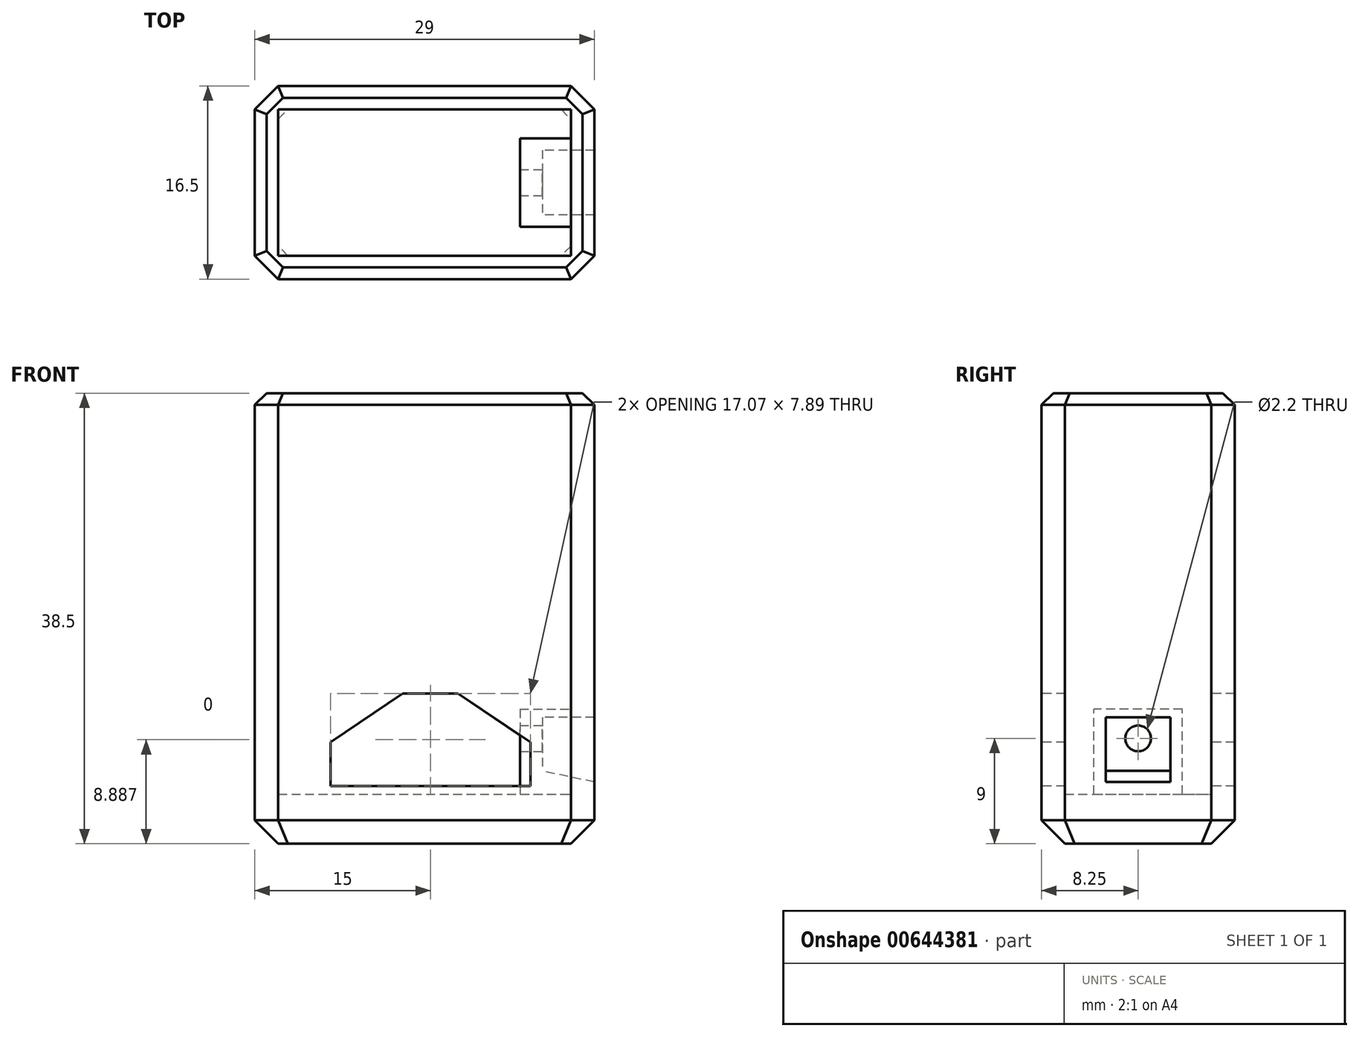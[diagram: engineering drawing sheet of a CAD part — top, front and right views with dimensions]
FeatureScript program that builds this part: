
annotation { "Feature Type Name" : "Feature", "Feature Type Description" : "" }
export const myFeature = defineFeature(function(context is Context, id is Id, definition is map)
    precondition{}
    {
        {
            var Q0;
            Q0=qCreatedBy(makeId("Top.planeOp"),FACE);
            var sketch = newSketch(context, id + "F0", { "sketchPlane" : qUnion([Q0])});
            skLineSegment(sketch, "E0.bottom", {"start": v(0, 0) * mm, "end": v(29, 0) * mm});
            skLineSegment(sketch, "E0.top", {"start": v(0, 16.5) * mm, "end": v(29, 16.5) * mm});
            skLineSegment(sketch, "E0.left", {"start": v(0, 0) * mm, "end": v(0, 16.5) * mm});
            skLineSegment(sketch, "E0.right", {"start": v(29, 0) * mm, "end": v(29, 16.5) * mm});
            skSolve(sketch);
        }
        {
            var Q0;
            Q0=makeQuery(id+"F0.imprint","IMPRINT",FACE,{"disambiguationData":[TD([[makeQuery(id+"F0.imprint","IMPRINT",EDGE,{"derivedFrom":sQuery(id+"F0.wireOp",EDGE,"E0.bottom")}),1.0]])]});
            extrude(context, id + "F1", {"entities" : qUnion([Q0]), "depth" : 38.5 * mm, "offsetDistance" : 25 * mm});
        }
        {
            var Q0;
            Q0=makeQuery(id+"F1.opExtrude","CAP_FACE",FACE,{"disambiguationData":[OSD([sQuery(id+"F0.wireOp",EDGE,"E0.bottom"),sQuery(id+"F0.wireOp",EDGE,"E0.top"),sQuery(id+"F0.wireOp",EDGE,"E0.left"),sQuery(id+"F0.wireOp",EDGE,"E0.right")])],"isStart":false});
            shell(context, id + "F2", {"entities" : qUnion([Q0]), "thickness" : 2 * mm});
        }
        {
            var Q0;
            Q0=makeQuery(id+"F2.opShell","OFFSET_FACE",FACE,{"disambiguationData":[OSD([sQuery(id+"F0.wireOp",EDGE,"E0.bottom"),sQuery(id+"F0.wireOp",EDGE,"E0.top"),sQuery(id+"F0.wireOp",EDGE,"E0.left"),sQuery(id+"F0.wireOp",EDGE,"E0.right")])]});
            extrude(context, id + "F3", {"entities" : qUnion([Q0]), "operationType" : NewBodyOperationType.ADD, "depth" : 2.25 * mm, "offsetDistance" : 25 * mm});
        }
        {
            var Q0;
            Q0=makeQuery(id+"F1.opExtrude","SWEPT_EDGE",EDGE,{"disambiguationData":[OSD([sQuery(id+"F0.wireOp",EDGE,"E0.top"),sQuery(id+"F0.wireOp",EDGE,"E0.right")])]});
            var Q1;
            Q1=makeQuery(id+"F1.opExtrude","SWEPT_EDGE",EDGE,{"disambiguationData":[OSD([sQuery(id+"F0.wireOp",EDGE,"E0.bottom"),sQuery(id+"F0.wireOp",EDGE,"E0.right")])]});
            var Q2;
            Q2=makeQuery(id+"F1.opExtrude","SWEPT_EDGE",EDGE,{"disambiguationData":[OSD([sQuery(id+"F0.wireOp",EDGE,"E0.top"),sQuery(id+"F0.wireOp",EDGE,"E0.left")])]});
            var Q3;
            Q3=makeQuery(id+"F1.opExtrude","SWEPT_EDGE",EDGE,{"disambiguationData":[OSD([sQuery(id+"F0.wireOp",EDGE,"E0.bottom"),sQuery(id+"F0.wireOp",EDGE,"E0.left")])]});
            chamfer(context, id + "F4", {"entities" : qUnion([Q0, Q1, Q2, Q3]), "width" : 2 * mm, "tangentPropagation" : true});
        }
        {
            var Q0;
            Q0=makeQuery(id+"F1.opExtrude","CAP_FACE",FACE,{"disambiguationData":[OSD([sQuery(id+"F0.wireOp",EDGE,"E0.bottom"),sQuery(id+"F0.wireOp",EDGE,"E0.top"),sQuery(id+"F0.wireOp",EDGE,"E0.left"),sQuery(id+"F0.wireOp",EDGE,"E0.right")])],"isStart":true});
            chamfer(context, id + "F5", {"entities" : qUnion([Q0]), "width" : 2 * mm, "tangentPropagation" : true});
        }
        {
            var Q0;
            Q0=makeQuery(id+"F1.opExtrude","CAP_EDGE",EDGE,{"disambiguationData":[OSD([sQuery(id+"F0.wireOp",EDGE,"E0.bottom")])],"isStart":false});
            var Q1;
            {var subQ0=sQuery(id+"F0.wireOp",EDGE,"E0.left");var subQ1=sQuery(id+"F0.wireOp",EDGE,"E0.bottom");Q1=makeQuery(id+"F4.opChamfer","BLEND_EDGE",EDGE,{"blendedFrom":[makeQuery(id+"F1.opExtrude","SWEPT_EDGE",EDGE,{"disambiguationData":[OSD([subQ1,subQ0])]}),makeQuery(id+"F1.opExtrude","CAP_FACE",FACE,{"disambiguationData":[OSD([subQ1,sQuery(id+"F0.wireOp",EDGE,"E0.top"),subQ0,sQuery(id+"F0.wireOp",EDGE,"E0.right")])],"isStart":false})],"blendedInto":[makeQuery(id+"F1.opExtrude","CAP_FACE",FACE,{"disambiguationData":[OSD([subQ1,sQuery(id+"F0.wireOp",EDGE,"E0.top"),subQ0,sQuery(id+"F0.wireOp",EDGE,"E0.right")])],"isStart":false})]});}
            var Q2;
            Q2=makeQuery(id+"F1.opExtrude","CAP_EDGE",EDGE,{"disambiguationData":[OSD([sQuery(id+"F0.wireOp",EDGE,"E0.left")])],"isStart":false});
            var Q3;
            {var subQ0=sQuery(id+"F0.wireOp",EDGE,"E0.left");var subQ1=sQuery(id+"F0.wireOp",EDGE,"E0.top");Q3=makeQuery(id+"F4.opChamfer","BLEND_EDGE",EDGE,{"blendedFrom":[makeQuery(id+"F1.opExtrude","SWEPT_EDGE",EDGE,{"disambiguationData":[OSD([subQ1,subQ0])]}),makeQuery(id+"F1.opExtrude","CAP_FACE",FACE,{"disambiguationData":[OSD([sQuery(id+"F0.wireOp",EDGE,"E0.bottom"),subQ1,subQ0,sQuery(id+"F0.wireOp",EDGE,"E0.right")])],"isStart":false})],"blendedInto":[makeQuery(id+"F1.opExtrude","CAP_FACE",FACE,{"disambiguationData":[OSD([sQuery(id+"F0.wireOp",EDGE,"E0.bottom"),subQ1,subQ0,sQuery(id+"F0.wireOp",EDGE,"E0.right")])],"isStart":false})]});}
            var Q4;
            Q4=makeQuery(id+"F1.opExtrude","CAP_EDGE",EDGE,{"disambiguationData":[OSD([sQuery(id+"F0.wireOp",EDGE,"E0.top")])],"isStart":false});
            var Q5;
            {var subQ0=sQuery(id+"F0.wireOp",EDGE,"E0.right");var subQ1=sQuery(id+"F0.wireOp",EDGE,"E0.top");Q5=makeQuery(id+"F4.opChamfer","BLEND_EDGE",EDGE,{"blendedFrom":[makeQuery(id+"F1.opExtrude","SWEPT_EDGE",EDGE,{"disambiguationData":[OSD([subQ1,subQ0])]}),makeQuery(id+"F1.opExtrude","CAP_FACE",FACE,{"disambiguationData":[OSD([sQuery(id+"F0.wireOp",EDGE,"E0.bottom"),subQ1,sQuery(id+"F0.wireOp",EDGE,"E0.left"),subQ0])],"isStart":false})],"blendedInto":[makeQuery(id+"F1.opExtrude","CAP_FACE",FACE,{"disambiguationData":[OSD([sQuery(id+"F0.wireOp",EDGE,"E0.bottom"),subQ1,sQuery(id+"F0.wireOp",EDGE,"E0.left"),subQ0])],"isStart":false})]});}
            var Q6;
            Q6=makeQuery(id+"F1.opExtrude","CAP_EDGE",EDGE,{"disambiguationData":[OSD([sQuery(id+"F0.wireOp",EDGE,"E0.right")])],"isStart":false});
            var Q7;
            {var subQ0=sQuery(id+"F0.wireOp",EDGE,"E0.right");var subQ1=sQuery(id+"F0.wireOp",EDGE,"E0.bottom");Q7=makeQuery(id+"F4.opChamfer","BLEND_EDGE",EDGE,{"blendedFrom":[makeQuery(id+"F1.opExtrude","SWEPT_EDGE",EDGE,{"disambiguationData":[OSD([subQ1,subQ0])]}),makeQuery(id+"F1.opExtrude","CAP_FACE",FACE,{"disambiguationData":[OSD([subQ1,sQuery(id+"F0.wireOp",EDGE,"E0.top"),sQuery(id+"F0.wireOp",EDGE,"E0.left"),subQ0])],"isStart":false})],"blendedInto":[makeQuery(id+"F1.opExtrude","CAP_FACE",FACE,{"disambiguationData":[OSD([subQ1,sQuery(id+"F0.wireOp",EDGE,"E0.top"),sQuery(id+"F0.wireOp",EDGE,"E0.left"),subQ0])],"isStart":false})]});}
            chamfer(context, id + "F6", {"entities" : qUnion([Q0, Q1, Q2, Q3, Q4, Q5, Q6, Q7]), "width" : 1 * mm, "tangentPropagation" : true});
        }
        {
            var Q0;
            Q0=makeQuery(id+"F1.opExtrude","SWEPT_FACE",FACE,{"disambiguationData":[OSD([sQuery(id+"F0.wireOp",EDGE,"E0.bottom")])]});
            var sketch = newSketch(context, id + "F7", { "sketchPlane" : qUnion([Q0])});
            skLineSegment(sketch, "E1", {"start": v(12.63, 12.83) * mm, "end": v(17.36, 12.83) * mm});
            skLineSegment(sketch, "E2", {"start": v(23.54, 8.67) * mm, "end": v(17.36, 12.83) * mm});
            skLineSegment(sketch, "E3", {"start": v(23.54, 8.67) * mm, "end": v(23.54, 4.94) * mm});
            skLineSegment(sketch, "E4", {"start": v(23.54, 4.94) * mm, "end": v(6.46, 4.94) * mm});
            skLineSegment(sketch, "E5", {"start": v(6.46, 4.94) * mm, "end": v(6.46, 8.67) * mm});
            skLineSegment(sketch, "E6", {"start": v(6.46, 8.67) * mm, "end": v(12.63, 12.83) * mm});
            skSolve(sketch);
        }
        {
            var Q0;
            Q0=makeQuery(id+"F7.imprint","IMPRINT",FACE,{"disambiguationData":[TD([[makeQuery(id+"F7.imprint","IMPRINT",EDGE,{"derivedFrom":sQuery(id+"F7.wireOp",EDGE,"E1")}),-1.0]])]});
            extrude(context, id + "F8", {"entities" : qUnion([Q0]), "operationType" : NewBodyOperationType.REMOVE, "endBound" : BoundingType.THROUGH_ALL, "oppositeDirection" : true, "depth" : 25 * mm, "offsetDistance" : 25 * mm});
        }
        {
            var Q0;
            Q0=makeQuery(id+"F1.opExtrude","SWEPT_FACE",FACE,{"disambiguationData":[OSD([sQuery(id+"F0.wireOp",EDGE,"E0.right")])]});
            var sketch = newSketch(context, id + "F9", { "sketchPlane" : qUnion([Q0])});
            skLineSegment(sketch, "E7.bottom", {"start": v(4.48, 11.5) * mm, "end": v(12.02, 11.5) * mm});
            skLineSegment(sketch, "E7.top", {"start": v(4.48, 4.25) * mm, "end": v(12.02, 4.25) * mm});
            skLineSegment(sketch, "E7.left", {"start": v(4.48, 11.5) * mm, "end": v(4.48, 4.25) * mm});
            skLineSegment(sketch, "E7.right", {"start": v(12.02, 11.5) * mm, "end": v(12.02, 4.25) * mm});
            skCircle(sketch, "E8", {"center": v(8.25, 9) * mm, "radius": 1.1 * mm});
            skSolve(sketch);
        }
        {
            var Q0;
            Q0 = qSketchRegion(id + "F9", true);
            extrude(context, id + "F10", {"entities" : qUnion([Q0]), "operationType" : NewBodyOperationType.ADD, "oppositeDirection" : true, "depth" : 6.35 * mm, "offsetDistance" : 25 * mm});
        }
        {
            var Q0;
            Q0=makeQuery(id+"F1.opExtrude","SWEPT_FACE",FACE,{"disambiguationData":[OSD([sQuery(id+"F0.wireOp",EDGE,"E0.right")])]});
            var sketch = newSketch(context, id + "F11", { "sketchPlane" : qUnion([Q0])});
            skLineSegment(sketch, "E9.bottom", {"start": v(5.48, 10.8) * mm, "end": v(11.02, 10.8) * mm});
            skLineSegment(sketch, "E9.top", {"start": v(5.48, 5.27) * mm, "end": v(11.02, 5.27) * mm});
            skLineSegment(sketch, "E9.left", {"start": v(5.48, 10.8) * mm, "end": v(5.48, 5.27) * mm});
            skLineSegment(sketch, "E9.right", {"start": v(11.02, 10.8) * mm, "end": v(11.02, 5.27) * mm});
            skSolve(sketch);
        }
        {
            var Q0;
            Q0=makeQuery(id+"F11.imprint","IMPRINT",FACE,{"disambiguationData":[TD([[makeQuery(id+"F11.imprint","IMPRINT",EDGE,{"derivedFrom":sQuery(id+"F11.wireOp",EDGE,"E9.bottom")}),1.0]])]});
            cPlane(context, id + "F12", {"entities" : qUnion([Q0]), "cplaneType" : CPlaneType.OFFSET, "offset" : 4.45 * mm, "oppositeDirection" : true, "width" : 150 * mm, "height" : 150 * mm});
        }
        {
            var Q0;
            Q0=qCreatedBy(id+"F12.planeOp",FACE);
            var sketch = newSketch(context, id + "F13", { "sketchPlane" : qUnion([Q0])});
            skLineSegment(sketch, "E10.bottom", {"start": v(11.02, 10.8) * mm, "end": v(5.48, 10.8) * mm});
            skLineSegment(sketch, "E10.top", {"start": v(11.02, 6.22) * mm, "end": v(5.48, 6.22) * mm});
            skLineSegment(sketch, "E10.left", {"start": v(11.02, 10.8) * mm, "end": v(11.02, 6.22) * mm});
            skLineSegment(sketch, "E10.right", {"start": v(5.48, 10.8) * mm, "end": v(5.48, 6.22) * mm});
            skSolve(sketch);
        }
        {
            var Q1;
            Q1 = qSketchRegion(id + "F11", true);
            var Q2;
            Q2 = qSketchRegion(id + "F13", true);
            loft(context, id + "F14", {"operationType" : NewBodyOperationType.REMOVE, "sheetProfilesArray" : [{ "sheetProfileEntities" : qUnion([Q1]) }, { "sheetProfileEntities" : qUnion([Q2]) }]});
        }
    });
